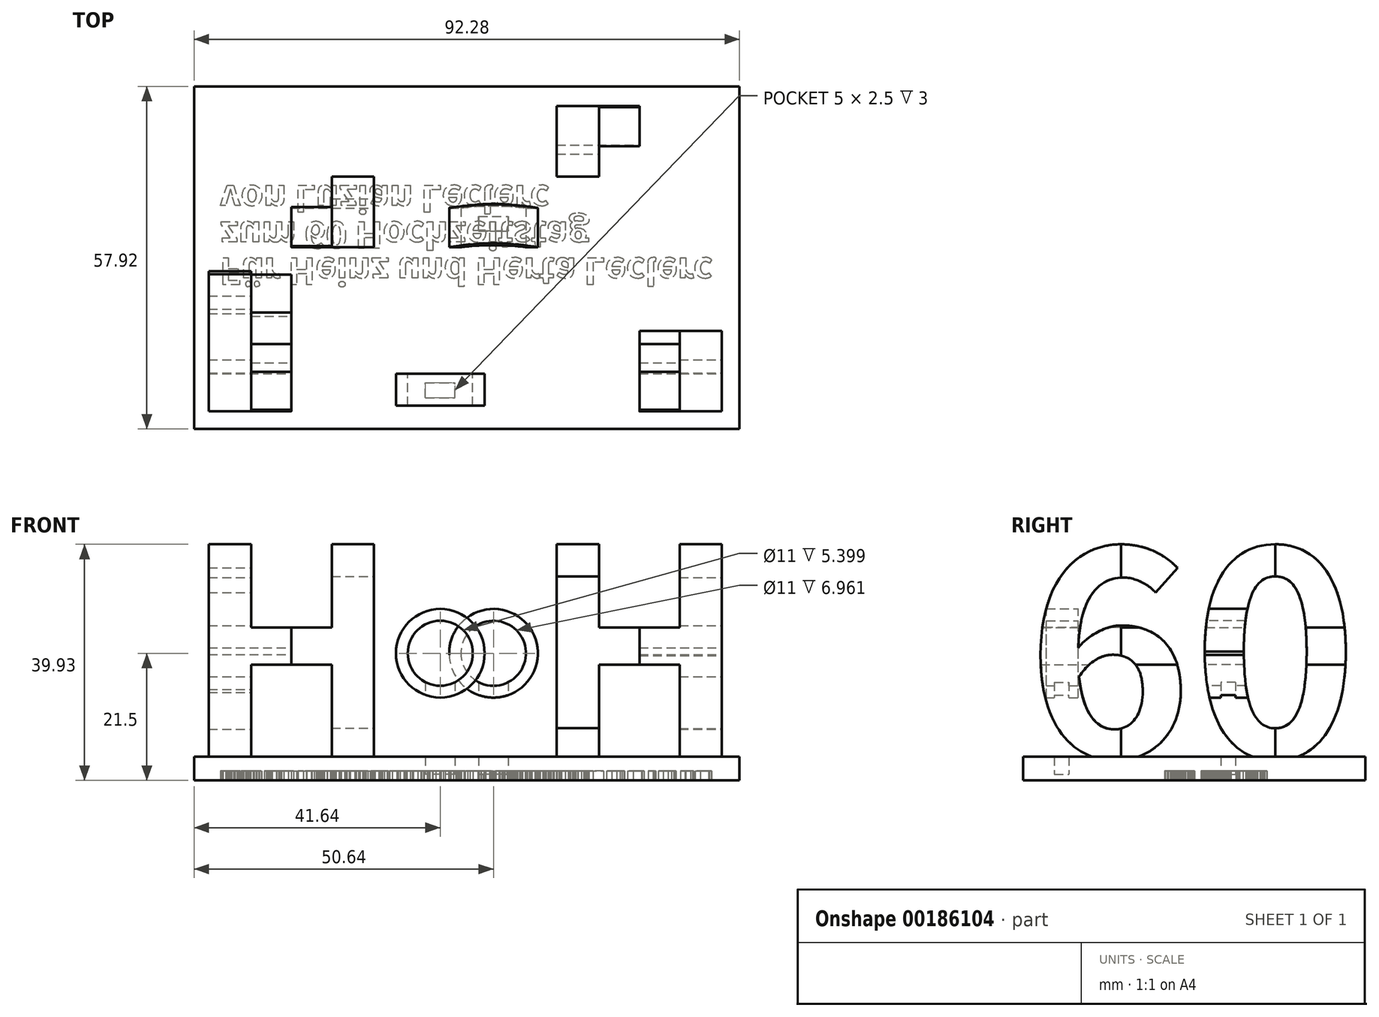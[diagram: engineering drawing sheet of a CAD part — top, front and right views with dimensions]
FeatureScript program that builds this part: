
annotation { "Feature Type Name" : "Feature", "Feature Type Description" : "" }
export const myFeature = defineFeature(function(context is Context, id is Id, definition is map)
    precondition{}
    {
        {
            var Q0;
            Q0=qCreatedBy(makeId("Front.planeOp"),FACE);
            var sketch = newSketch(context, id + "F0", { "sketchPlane" : qUnion([Q0])});
            skText(sketch, "E0", { "text": "H  H", "fontName": "NotoSansCJKsc-Bold.otf"});
            const initialGuessF0  = {"E0": [-0.0481, 0, 1, 0, 0.035]};
            skSetInitialGuess(sketch, initialGuessF0);
            skSolve(sketch);
        }
        {
            var Q0;
            Q0=qCreatedBy(makeId("Front.planeOp"),FACE);
            var sketch = newSketch(context, id + "F1", { "sketchPlane" : qUnion([Q0])});
            skCircle(sketch, "E1", {"center": v(4.5, 17.5) * mm, "radius": 7.5 * mm});
            skCircle(sketch, "E2", {"center": v(4.5, 17.5) * mm, "radius": 5.5 * mm});
            skSolve(sketch);
        }
        {
            var Q0;
            Q0 = qSketchRegion(id + "F1", true);
            extrude(context, id + "F2", {"entities" : qUnion([Q0]), "oppositeDirection" : true, "depth" : 25 * mm});
        }
        {
            var Q0;
            Q0=qCreatedBy(makeId("Front.planeOp"),FACE);
            var sketch = newSketch(context, id + "F3", { "sketchPlane" : qUnion([Q0])});
            skCircle(sketch, "E3", {"center": v(-4.5, 17.5) * mm, "radius": 7.5 * mm});
            skCircle(sketch, "E4", {"center": v(-4.5, 17.5) * mm, "radius": 5.5 * mm});
            skSolve(sketch);
        }
        {
            var Q0;
            Q0 = qSketchRegion(id + "F3", true);
            extrude(context, id + "F4", {"entities" : qUnion([Q0]), "operationType" : NewBodyOperationType.ADD, "depth" : 25 * mm});
        }
        {
            var Q0;
            Q0=qSketchRegion(id+"F0",true);
            extrude(context, id + "F5", {"entities" : qUnion([Q0]), "depth" : 50 * mm, "hasSecondDirection" : true, "secondDirectionOppositeDirection" : true, "secondDirectionDepth" : 50 * mm});
        }
        {
            var Q0;
            Q0=qCreatedBy(makeId("Right.planeOp"),FACE);
            var sketch = newSketch(context, id + "F6", { "sketchPlane" : qUnion([Q0])});
            skText(sketch, "E5", { "text": "60", "fontName": "NotoSansCJKsc-Bold.otf"});
            const initialGuessF6  = {"E5": [-0.02837, 0, 1, 0, 0.03431]};
            skSetInitialGuess(sketch, initialGuessF6);
            skSolve(sketch);
        }
        {
            var Q0;
            Q0=qSketchRegion(id+"F6",true);
            extrude(context, id + "F7", {"entities" : qUnion([Q0]), "operationType" : NewBodyOperationType.INTERSECT, "endBound" : BoundingType.THROUGH_ALL, "oppositeDirection" : true, "depth" : 25 * mm, "hasSecondDirection" : true, "secondDirectionBound" : SecondDirectionBoundingType.THROUGH_ALL, "secondDirectionOppositeDirection" : false, "secondDirectionDepth" : 25 * mm});
        }
        {
            var Q0;
            Q0=qCreatedBy(makeId("Top.planeOp"),FACE);
            var sketch = newSketch(context, id + "F8", { "sketchPlane" : qUnion([Q0])});
            skLineSegment(sketch, "E6.bottom", {"start": v(-15.73, 1.8) * mm, "end": v(-29.7, 1.8) * mm});
            skLineSegment(sketch, "E6.top", {"start": v(-15.73, 13.76) * mm, "end": v(-29.7, 13.76) * mm});
            skLineSegment(sketch, "E6.left", {"start": v(-15.73, 1.8) * mm, "end": v(-15.73, 13.76) * mm});
            skLineSegment(sketch, "E6.right", {"start": v(-29.7, 1.8) * mm, "end": v(-29.7, 13.76) * mm});
            skLineSegment(sketch, "E7.bottom", {"start": v(-43.68, -2.26) * mm, "end": v(-29.7, -2.26) * mm});
            skLineSegment(sketch, "E7.top", {"start": v(-43.68, -25.99) * mm, "end": v(-29.7, -25.99) * mm});
            skLineSegment(sketch, "E7.left", {"start": v(-43.68, -2.26) * mm, "end": v(-43.68, -25.99) * mm});
            skLineSegment(sketch, "E7.right", {"start": v(-29.7, -2.26) * mm, "end": v(-29.7, -25.99) * mm});
            skLineSegment(sketch, "E8.bottom", {"start": v(15.2, 25.67) * mm, "end": v(29.2, 25.67) * mm});
            skLineSegment(sketch, "E8.top", {"start": v(15.2, 13.76) * mm, "end": v(29.2, 13.76) * mm});
            skLineSegment(sketch, "E8.left", {"start": v(15.2, 25.67) * mm, "end": v(15.2, 13.76) * mm});
            skLineSegment(sketch, "E8.right", {"start": v(29.2, 25.67) * mm, "end": v(29.2, 13.76) * mm});
            skLineSegment(sketch, "E9.bottom", {"start": v(43.14, -25.99) * mm, "end": v(29.2, -25.99) * mm});
            skLineSegment(sketch, "E9.top", {"start": v(43.14, -12.36) * mm, "end": v(29.2, -12.36) * mm});
            skLineSegment(sketch, "E9.left", {"start": v(43.14, -25.99) * mm, "end": v(43.14, -12.36) * mm});
            skLineSegment(sketch, "E9.right", {"start": v(29.2, -25.99) * mm, "end": v(29.2, -12.36) * mm});
            skLineSegment(sketch, "E10.bottom", {"start": v(3.87, -25) * mm, "end": v(-12.6, -25) * mm});
            skLineSegment(sketch, "E10.top", {"start": v(3.87, -19.6) * mm, "end": v(-12.6, -19.6) * mm});
            skLineSegment(sketch, "E10.left", {"start": v(3.87, -25) * mm, "end": v(3.87, -19.6) * mm});
            skLineSegment(sketch, "E10.right", {"start": v(-12.6, -25) * mm, "end": v(-12.6, -19.6) * mm});
            skLineSegment(sketch, "E11.bottom", {"start": v(-3, 1.8) * mm, "end": v(12, 1.8) * mm});
            skLineSegment(sketch, "E11.top", {"start": v(-3, 9.12) * mm, "end": v(12, 9.12) * mm});
            skLineSegment(sketch, "E11.left", {"start": v(-3, 1.8) * mm, "end": v(-3, 9.12) * mm});
            skLineSegment(sketch, "E11.right", {"start": v(12, 1.8) * mm, "end": v(12, 9.12) * mm});
            skSolve(sketch);
        }
        {
            var Q0;
            Q0 = qSketchRegion(id + "F8", true);
            extrude(context, id + "F9", {"entities" : qUnion([Q0]), "operationType" : NewBodyOperationType.INTERSECT, "endBound" : BoundingType.THROUGH_ALL, "depth" : 25 * mm});
        }
        {
            var Q0;
            Q0=qCreatedBy(makeId("Top.planeOp"),FACE);
            var sketch = newSketch(context, id + "F10", { "sketchPlane" : qUnion([Q0])});
            skLineSegment(sketch, "E12.bottom", {"start": v(46.14, -28.96) * mm, "end": v(-46.14, -28.96) * mm});
            skLineSegment(sketch, "E12.top", {"start": v(46.14, 28.96) * mm, "end": v(-46.14, 28.96) * mm});
            skLineSegment(sketch, "E12.left", {"start": v(46.14, -28.96) * mm, "end": v(46.14, 28.96) * mm});
            skLineSegment(sketch, "E12.right", {"start": v(-46.14, -28.96) * mm, "end": v(-46.14, 28.96) * mm});
            skPoint(sketch, "E12.middle", {"position": v(0, 0) * mm});
            skSolve(sketch);
        }
        {
            var Q0;
            Q0 = qSketchRegion(id + "F10", true);
            extrude(context, id + "F11", {"entities" : qUnion([Q0]), "operationType" : NewBodyOperationType.ADD, "oppositeDirection" : true, "depth" : 4 * mm});
        }
        {
            var Q0;
            Q0=makeQuery(id+"F11.opExtrude","CAP_FACE",FACE,{"disambiguationData":[OSD([sQuery(id+"F10.wireOp",EDGE,"E12.bottom"),sQuery(id+"F10.wireOp",EDGE,"E12.top"),sQuery(id+"F10.wireOp",EDGE,"E12.left"),sQuery(id+"F10.wireOp",EDGE,"E12.right")])],"isStart":true});
            var sketch = newSketch(context, id + "F12", { "sketchPlane" : qUnion([Q0])});
            skLineSegment(sketch, "E13.bottom", {"start": v(-2, -23.66) * mm, "end": v(-7, -23.66) * mm});
            skLineSegment(sketch, "E13.top", {"start": v(-2, -21.16) * mm, "end": v(-7, -21.16) * mm});
            skLineSegment(sketch, "E13.left", {"start": v(-2, -23.66) * mm, "end": v(-2, -21.16) * mm});
            skLineSegment(sketch, "E13.right", {"start": v(-7, -23.66) * mm, "end": v(-7, -21.16) * mm});
            skPoint(sketch, "E13.middle", {"position": v(-4.5, -22.41) * mm});
            skLineSegment(sketch, "E14", {"start": v(-4.5, -22.41) * mm, "end": v(-4.5, -19.6) * mm, "construction": true});
            skLineSegment(sketch, "E15", {"start": v(-4.5, -19.6) * mm, "end": v(-4.5, -22.41) * mm, "construction": true});
            skLineSegment(sketch, "E16", {"start": v(-4.5, -22.41) * mm, "end": v(-4.5, -25.23) * mm, "construction": true});
            skPoint(sketch, "E16.endSnap0", {"position": v(-4.5, -23.66) * mm});
            skPoint(sketch, "E17.endSnap0", {"position": v(-7, -22.41) * mm});
            skLineSegment(sketch, "E18.bottom", {"start": v(7, 4.52) * mm, "end": v(2, 4.52) * mm});
            skLineSegment(sketch, "E18.top", {"start": v(7, 7.02) * mm, "end": v(2, 7.02) * mm});
            skLineSegment(sketch, "E18.left", {"start": v(7, 4.52) * mm, "end": v(7, 7.02) * mm});
            skLineSegment(sketch, "E18.right", {"start": v(2, 4.52) * mm, "end": v(2, 7.02) * mm});
            skPoint(sketch, "E18.middle", {"position": v(4.5, 5.77) * mm});
            skPoint(sketch, "E19.endSnap0", {"position": v(4.5, 4.52) * mm});
            skPoint(sketch, "E20.endSnap0", {"position": v(2, 5.77) * mm});
            skSolve(sketch);
        }
        {
            var Q0;
            Q0 = qSketchRegion(id + "F12", true);
            extrude(context, id + "F13", {"entities" : qUnion([Q0]), "operationType" : NewBodyOperationType.REMOVE, "depth" : 13 * mm, "hasSecondDirection" : true, "secondDirectionOppositeDirection" : true, "secondDirectionDepth" : 3 * mm});
        }
        {
            var Q0;
            Q0=makeQuery(id+"F11.opExtrude","CAP_FACE",FACE,{"disambiguationData":[OSD([sQuery(id+"F10.wireOp",EDGE,"E12.bottom"),sQuery(id+"F10.wireOp",EDGE,"E12.top"),sQuery(id+"F10.wireOp",EDGE,"E12.left"),sQuery(id+"F10.wireOp",EDGE,"E12.right")])],"isStart":false});
            var sketch = newSketch(context, id + "F14", { "sketchPlane" : qUnion([Q0])});
            skText(sketch, "E21", { "text": "Für Heinz und Herta Leclerc\nzum 60 Hochzeitstag\nvon Luzian Leclerc", "fontName": "NotoSansCJKsc-Bold.otf"});
            const initialGuessF14  = {"E21": [-0.0418, 0, 1, 0, 0.00441]};
            skSetInitialGuess(sketch, initialGuessF14);
            skSolve(sketch);
        }
        {
            var Q0;
            Q0 = qSketchRegion(id + "F14", true);
            extrude(context, id + "F15", {"entities" : qUnion([Q0]), "operationType" : NewBodyOperationType.REMOVE, "oppositeDirection" : true, "depth" : 1.6 * mm});
        }
    });
